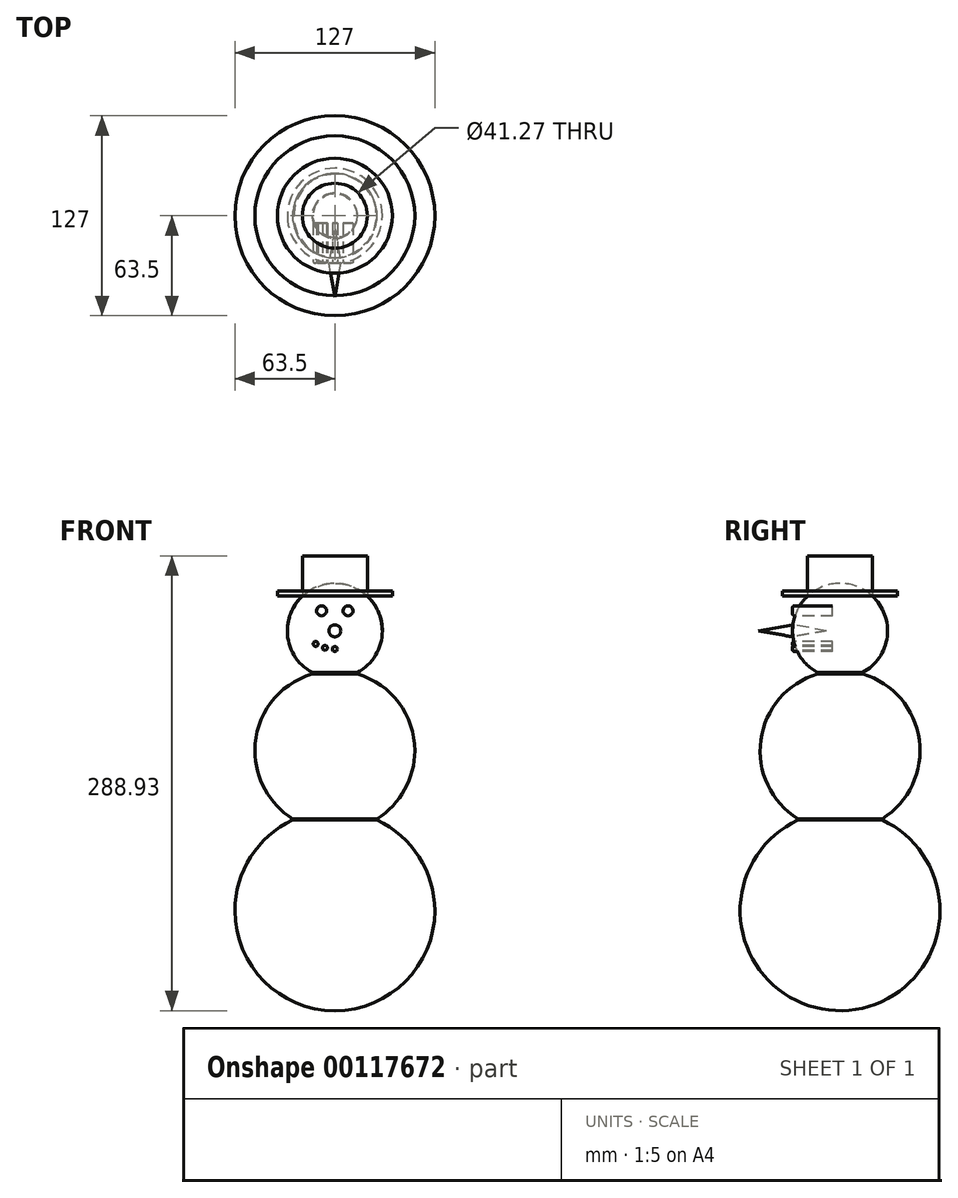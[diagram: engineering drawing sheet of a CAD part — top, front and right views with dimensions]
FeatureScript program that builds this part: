
annotation { "Feature Type Name" : "Feature", "Feature Type Description" : "" }
export const myFeature = defineFeature(function(context is Context, id is Id, definition is map)
    precondition{}
    {
        {
            var Q0;
            Q0=qCreatedBy(makeId("Top.planeOp"),FACE);
            var sketch = newSketch(context, id + "F0", { "sketchPlane" : qUnion([Q0])});
            skArc(sketch, "E0", {"start": v(63.5, 0) * mm, "mid": v(0, 63.5) * mm, "end": v(-63.5, 0) * mm});
            skLineSegment(sketch, "E1", {"start": v(-63.5, 0) * mm, "end": v(63.5, 0) * mm});
            skSolve(sketch);
        }
        {
            var Q0;
            Q0 = qSketchRegion(id + "F0", true);
            var Q1;
            Q1=sQuery(id+"F0.wireOp",EDGE,"E1");
            revolve(context, id + "F1", {"entities" : qUnion([Q0]), "axis" : qUnion([Q1]), "revolveType" : RevolveType.FULL});
        }
        {
            var Q0;
            Q0=qCreatedBy(makeId("Front.planeOp"),FACE);
            var sketch = newSketch(context, id + "F2", { "sketchPlane" : qUnion([Q0])});
            skLineSegment(sketch, "E2", {"start": v(0, 0) * mm, "end": v(0, 50.8) * mm});
            skArc(sketch, "E3", {"start": v(-50.8, 101.6) * mm, "mid": v(0, 50.8) * mm, "end": v(50.8, 101.6) * mm});
            skLineSegment(sketch, "E4", {"start": v(0, 101.6) * mm, "end": v(50.8, 101.6) * mm});
            skLineSegment(sketch, "E5", {"start": v(50.8, 101.6) * mm, "end": v(0, 101.6) * mm});
            skLineSegment(sketch, "E6", {"start": v(-50.8, 101.6) * mm, "end": v(0, 101.6) * mm});
            skSolve(sketch);
        }
        {
            var Q0;
            Q0 = qSketchRegion(id + "F2", true);
            var Q1;
            Q1=sQuery(id+"F2.wireOp",EDGE,"E5");
            revolve(context, id + "F3", {"operationType" : NewBodyOperationType.ADD, "entities" : qUnion([Q0]), "axis" : qUnion([Q1]), "revolveType" : RevolveType.FULL});
        }
        {
            var Q0;
            Q0=qCreatedBy(makeId("Front.planeOp"),FACE);
            var sketch = newSketch(context, id + "F4", { "sketchPlane" : qUnion([Q0])});
            skLineSegment(sketch, "E7", {"start": v(0, 177.8) * mm, "end": v(0, 0) * mm});
            skArc(sketch, "E8", {"start": v(30.16, 177.8) * mm, "mid": v(0, 207.96) * mm, "end": v(-30.16, 177.8) * mm});
            skLineSegment(sketch, "E9", {"start": v(0, 177.8) * mm, "end": v(30.16, 177.8) * mm});
            skLineSegment(sketch, "E10", {"start": v(0, 177.8) * mm, "end": v(-30.16, 177.8) * mm});
            skSolve(sketch);
        }
        {
            var Q0;
            Q0 = qSketchRegion(id + "F4", true);
            var Q1;
            Q1=sQuery(id+"F4.wireOp",EDGE,"E10");
            revolve(context, id + "F5", {"operationType" : NewBodyOperationType.ADD, "entities" : qUnion([Q0]), "axis" : qUnion([Q1]), "revolveType" : RevolveType.FULL});
        }
        {
            var Q0;
            Q0=makeQuery(id+"F3.boolean.opBoolean","INTERSECT",EDGE,{"derivedFrom":[makeQuery(id+"F1.opRevolve","SWEPT_FACE",FACE,{"disambiguationData":[OSD([sQuery(id+"F0.wireOp",EDGE,"E0")])]}),makeQuery(id+"F3.opRevolve","SWEPT_FACE",FACE,{"disambiguationData":[OSD([sQuery(id+"F2.wireOp",EDGE,"E3")])]})]});
            var Q1;
            Q1=makeQuery(id+"F5.boolean.opBoolean","INTERSECT",EDGE,{"derivedFrom":[makeQuery(id+"F3.opRevolve","SWEPT_FACE",FACE,{"disambiguationData":[OSD([sQuery(id+"F2.wireOp",EDGE,"E3")])]}),makeQuery(id+"F5.opRevolve","SWEPT_FACE",FACE,{"disambiguationData":[OSD([sQuery(id+"F4.wireOp",EDGE,"E8")])]})]});
            fillet(context, id + "F6", {"entities" : qUnion([Q0, Q1]), "radius" : 0.5 * mm, "tangentPropagation" : true, "allowEdgeOverflow" : false});
        }
        {
            var Q0;
            Q0=qCreatedBy(makeId("Front.planeOp"),FACE);
            cPlane(context, id + "F7", {"entities" : qUnion([Q0]), "cplaneType" : CPlaneType.OFFSET, "offset" : 30.16 * mm, "width" : 152.4 * mm, "height" : 152.4 * mm});
        }
        {
            var Q0;
            Q0=qCreatedBy(id+"F7.planeOp",FACE);
            var sketch = newSketch(context, id + "F8", { "sketchPlane" : qUnion([Q0])});
            skLineSegment(sketch, "E11", {"start": v(0, 0) * mm, "end": v(0, 177.8) * mm});
            skCircle(sketch, "E12", {"center": v(-8.4, 190.52) * mm, "radius": 3.18 * mm});
            skCircle(sketch, "E13", {"center": v(8.4, 190.52) * mm, "radius": 3.18 * mm});
            skCircle(sketch, "E14", {"center": v(0, 177.8) * mm, "radius": 3.81 * mm});
            skCircle(sketch, "E15", {"center": v(0, 166.2) * mm, "radius": 1.59 * mm});
            skCircle(sketch, "E16.1.0", {"center": v(-6.3, 167.03) * mm, "radius": 1.59 * mm});
            skCircle(sketch, "E16.2.0", {"center": v(-12.16, 169.46) * mm, "radius": 1.59 * mm});
            skPoint(sketch, "E16.center", {"position": v(0, 190.52) * mm});
            skCircle(sketch, "E17.MirrorC", {"center": v(6.3, 167.03) * mm, "radius": 1.59 * mm});
            skCircle(sketch, "E18.MirrorC", {"center": v(12.16, 169.46) * mm, "radius": 1.59 * mm});
            skSolve(sketch);
        }
        {
            var Q0;
            Q0=makeQuery(id+"F8.imprint","IMPRINT",FACE,{"disambiguationData":[TD([[makeQuery(id+"F8.imprint","IMPRINT",EDGE,{"derivedFrom":sQuery(id+"F8.wireOp",EDGE,"E12")}),1.0]])]});
            var Q1;
            Q1=makeQuery(id+"F8.imprint","IMPRINT",FACE,{"disambiguationData":[TD([[makeQuery(id+"F8.imprint","IMPRINT",EDGE,{"derivedFrom":sQuery(id+"F8.wireOp",EDGE,"E13")}),1.0]])]});
            var Q2;
            Q2=makeQuery(id+"F8.imprint","IMPRINT",FACE,{"disambiguationData":[TD([[makeQuery(id+"F8.imprint","IMPRINT",EDGE,{"derivedFrom":sQuery(id+"F8.wireOp",EDGE,"E16.2.0")}),1.0]])]});
            var Q3;
            Q3=makeQuery(id+"F8.imprint","IMPRINT",FACE,{"disambiguationData":[TD([[makeQuery(id+"F8.imprint","IMPRINT",EDGE,{"derivedFrom":sQuery(id+"F8.wireOp",EDGE,"E16.1.0")}),1.0]])]});
            var Q4;
            {var subQ0=sQuery(id+"F8.wireOp",EDGE,"E15");var subQ1=sQuery(id+"F8.wireOp",EDGE,"E11");var subQ2=makeQuery(id+"F8.imprint","INTERSECT",VERTEX,{"disambiguationData":[OD(0.0)],"derivedFrom":[subQ1,subQ0]});Q4=makeQuery(id+"F8.imprint","IMPRINT",FACE,{"disambiguationData":[TD([[makeQuery(id+"F8.imprint","IMPRINT",EDGE,{"disambiguationData":[TD([[subQ2,-1.0]])],"derivedFrom":subQ1}),-1.0]])]});}
            var Q5;
            Q5=makeQuery(id+"F8.imprint","IMPRINT",FACE,{"disambiguationData":[TD([[makeQuery(id+"F8.imprint","IMPRINT",EDGE,{"derivedFrom":sQuery(id+"F8.wireOp",EDGE,"E17.MirrorC")}),-1.0]])]});
            var Q6;
            Q6=makeQuery(id+"F8.imprint","IMPRINT",FACE,{"disambiguationData":[TD([[makeQuery(id+"F8.imprint","IMPRINT",EDGE,{"derivedFrom":sQuery(id+"F8.wireOp",EDGE,"E18.MirrorC")}),-1.0]])]});
            var Q7;
            {var subQ0=sQuery(id+"F8.wireOp",EDGE,"E15");var subQ1=sQuery(id+"F8.wireOp",EDGE,"E11");var subQ2=makeQuery(id+"F8.imprint","INTERSECT",VERTEX,{"disambiguationData":[OD(0.0)],"derivedFrom":[subQ1,subQ0]});Q7=makeQuery(id+"F8.imprint","IMPRINT",FACE,{"disambiguationData":[TD([[makeQuery(id+"F8.imprint","IMPRINT",EDGE,{"disambiguationData":[TD([[subQ2,-1.0]])],"derivedFrom":subQ1}),1.0]])]});}
            var Q8;
            Q8=sQuery(id+"F8.wireOp",EDGE,"E12");
            var Q9;
            Q9=sQuery(id+"F8.wireOp",EDGE,"E13");
            var Q10;
            Q10=sQuery(id+"F8.wireOp",EDGE,"E18.MirrorC");
            var Q11;
            Q11=sQuery(id+"F8.wireOp",EDGE,"E17.MirrorC");
            var Q12;
            Q12=sQuery(id+"F8.wireOp",EDGE,"E15");
            var Q13;
            Q13=sQuery(id+"F8.wireOp",EDGE,"E16.1.0");
            var Q14;
            Q14=sQuery(id+"F8.wireOp",EDGE,"E16.2.0");
            extrude(context, id + "F9", {"entities" : qUnion([Q0, Q1, Q2, Q3, Q4, Q5, Q6, Q7]), "surfaceEntities" : qUnion([Q8, Q9, Q10, Q11, Q12, Q13, Q14]), "oppositeDirection" : true, "depth" : 25.4 * mm});
        }
        {
            var Q0;
            Q0=makeQuery(id+"F9.opExtrude","CAP_EDGE",EDGE,{"disambiguationData":[OSD([sQuery(id+"F8.wireOp",EDGE,"E12")])],"isStart":true});
            var Q1;
            Q1=makeQuery(id+"F9.opExtrude","CAP_EDGE",EDGE,{"disambiguationData":[OSD([sQuery(id+"F8.wireOp",EDGE,"E13")])],"isStart":true});
            var Q2;
            Q2=makeQuery(id+"F9.opExtrude","CAP_EDGE",EDGE,{"disambiguationData":[OSD([sQuery(id+"F8.wireOp",EDGE,"E16.2.0")])],"isStart":true});
            var Q3;
            Q3=makeQuery(id+"F9.opExtrude","CAP_EDGE",EDGE,{"disambiguationData":[OSD([sQuery(id+"F8.wireOp",EDGE,"E16.1.0")])],"isStart":true});
            var Q4;
            Q4=makeQuery(id+"F9.opExtrude","CAP_EDGE",EDGE,{"disambiguationData":[OSD([sQuery(id+"F8.wireOp",EDGE,"E15")])],"isStart":true});
            var Q5;
            Q5=makeQuery(id+"F9.opExtrude","CAP_EDGE",EDGE,{"disambiguationData":[OSD([sQuery(id+"F8.wireOp",EDGE,"E17.MirrorC")])],"isStart":true});
            var Q6;
            Q6=makeQuery(id+"F9.opExtrude","CAP_EDGE",EDGE,{"disambiguationData":[OSD([sQuery(id+"F8.wireOp",EDGE,"E18.MirrorC")])],"isStart":true});
            fillet(context, id + "F10", {"entities" : qUnion([Q0, Q1, Q2, Q3, Q4, Q5, Q6]), "radius" : 1.27 * mm, "tangentPropagation" : true, "rho" : 0.5, "crossSection" : FilletCrossSection.CONIC, "allowEdgeOverflow" : false});
        }
        {
            var Q0;
            Q0=makeQuery(id+"F8.imprint","IMPRINT",FACE,{"disambiguationData":[TD([[makeQuery(id+"F8.imprint","IMPRINT",EDGE,{"derivedFrom":sQuery(id+"F8.wireOp",EDGE,"E14")}),1.0]])]});
            extrude(context, id + "F11", {"entities" : qUnion([Q0]), "endBound" : BoundingType.SYMMETRIC, "depth" : 50.8 * mm, "hasDraft" : true, "draftAngle" : 10 * degree, "draftPullDirection" : true});
        }
        {
            var Q0;
            Q0=qCreatedBy(makeId("Top.planeOp"),FACE);
            cPlane(context, id + "F12", {"entities" : qUnion([Q0]), "cplaneType" : CPlaneType.OFFSET, "offset" : 200.02 * mm, "width" : 152.4 * mm, "height" : 152.4 * mm});
        }
        {
            var Q0;
            Q0=qCreatedBy(id+"F12.planeOp",FACE);
            var sketch = newSketch(context, id + "F13", { "sketchPlane" : qUnion([Q0])});
            skCircle(sketch, "E19", {"center": v(0, 0) * mm, "radius": 36.51 * mm});
            skCircle(sketch, "E20", {"center": v(0, 0) * mm, "radius": 20.64 * mm});
            skSolve(sketch);
        }
        {
            var Q0;
            Q0 = qSketchRegion(id + "F13", true);
            extrude(context, id + "F14", {"entities" : qUnion([Q0]), "depth" : 3.17 * mm});
        }
        {
            var Q0;
            Q0=makeQuery(id+"F13.imprint","IMPRINT",FACE,{"disambiguationData":[TD([[makeQuery(id+"F13.imprint","IMPRINT",EDGE,{"derivedFrom":sQuery(id+"F13.wireOp",EDGE,"E20")}),1.0]])]});
            extrude(context, id + "F15", {"entities" : qUnion([Q0]), "depth" : 25.4 * mm});
        }
    });
